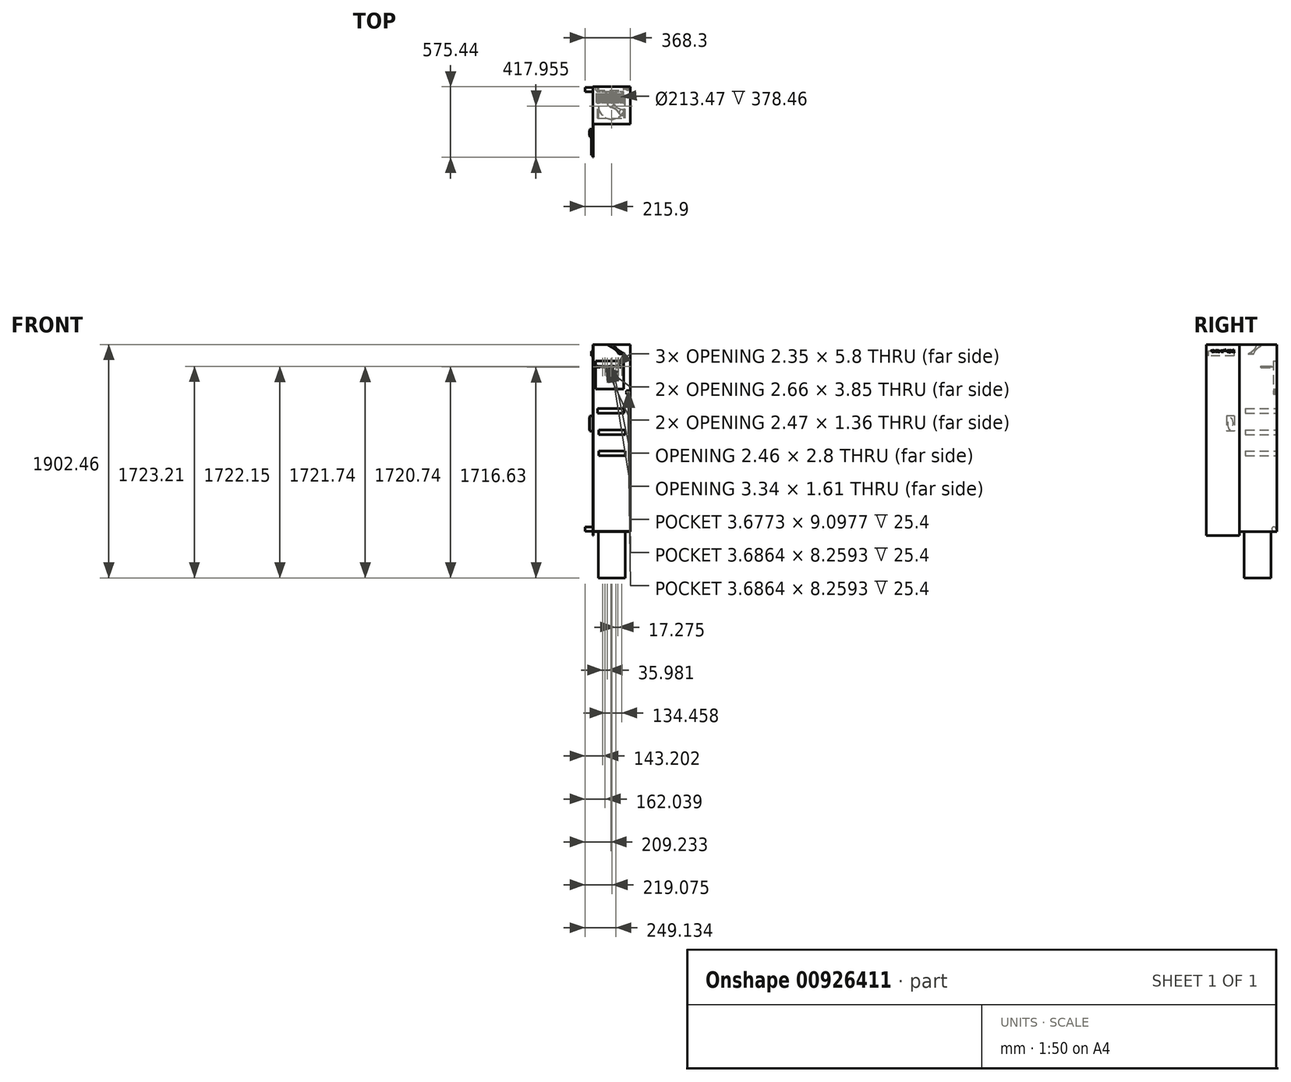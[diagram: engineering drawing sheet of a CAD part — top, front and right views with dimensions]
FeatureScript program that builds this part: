
annotation { "Feature Type Name" : "Feature", "Feature Type Description" : "" }
export const myFeature = defineFeature(function(context is Context, id is Id, definition is map)
    precondition{}
    {
        {
            var Q0;
            Q0=qCreatedBy(makeId("Front.planeOp"),FACE);
            var sketch = newSketch(context, id + "F0", { "sketchPlane" : qUnion([Q0])});
            skLineSegment(sketch, "E0.bottom", {"start": v(152.4, 762) * mm, "end": v(-152.4, 762) * mm});
            skLineSegment(sketch, "E0.top", {"start": v(152.4, -762) * mm, "end": v(-152.4, -762) * mm});
            skLineSegment(sketch, "E0.left", {"start": v(152.4, 762) * mm, "end": v(152.4, -762) * mm});
            skLineSegment(sketch, "E0.right", {"start": v(-152.4, 762) * mm, "end": v(-152.4, -762) * mm});
            skPoint(sketch, "E0.middle", {"position": v(0, 0) * mm});
            skSolve(sketch);
        }
        {
            var Q0;
            Q0=makeQuery(id+"F0.imprint","IMPRINT",FACE,{"disambiguationData":[TD([[makeQuery(id+"F0.imprint","IMPRINT",EDGE,{"derivedFrom":sQuery(id+"F0.wireOp",EDGE,"E0.bottom")}),1.0]])]});
            extrude(context, id + "F1", {"entities" : qUnion([Q0]), "depth" : 304.8 * mm, "offsetDistance" : 25.4 * mm});
        }
        {
            var Q0;
            Q0=makeQuery(id+"F1.opExtrude","CAP_FACE",FACE,{"disambiguationData":[OSD([sQuery(id+"F0.wireOp",EDGE,"E0.bottom"),sQuery(id+"F0.wireOp",EDGE,"E0.top"),sQuery(id+"F0.wireOp",EDGE,"E0.left"),sQuery(id+"F0.wireOp",EDGE,"E0.right")])],"isStart":false});
            shell(context, id + "F2", {"entities" : qUnion([Q0]), "thickness" : 2.54 * mm});
        }
        {
            var Q0;
            Q0=makeQuery(id+"F1.opExtrude","CAP_EDGE",EDGE,{"disambiguationData":[OSD([sQuery(id+"F0.wireOp",EDGE,"E0.right")])],"isStart":false});
            cPlane(context, id + "F3", {"entities" : qUnion([Q0]), "cplaneType" : CPlaneType.LINE_ANGLE, "offset" : 25.4 * mm, "angle" : 0 * degree, "width" : 152.4 * mm, "height" : 152.4 * mm});
        }
        {
            var Q0;
            Q0=qCreatedBy(id+"F3.planeOp",FACE);
            var sketch = newSketch(context, id + "F4", { "sketchPlane" : qUnion([Q0])});
            skLineSegment(sketch, "E1.bottom", {"start": v(304.8, 760.38) * mm, "end": v(575.44, 760.38) * mm});
            skLineSegment(sketch, "E1.top", {"start": v(304.8, -796.06) * mm, "end": v(575.44, -796.06) * mm});
            skLineSegment(sketch, "E1.left", {"start": v(304.8, 760.38) * mm, "end": v(304.8, -796.06) * mm});
            skLineSegment(sketch, "E1.right", {"start": v(575.44, 760.38) * mm, "end": v(575.44, -796.06) * mm});
            skSolve(sketch);
        }
        {
            var Q0;
            Q0=makeQuery(id+"F4.imprint","IMPRINT",FACE,{"disambiguationData":[TD([[makeQuery(id+"F4.imprint","IMPRINT",EDGE,{"derivedFrom":sQuery(id+"F4.wireOp",EDGE,"E1.bottom")}),-1.0]])]});
            extrude(context, id + "F5", {"entities" : qUnion([Q0]), "oppositeDirection" : true, "depth" : 2.54 * mm, "offsetDistance" : 25.4 * mm});
        }
        {
            var Q0;
            Q0=makeQuery(id+"F5.opExtrude","CAP_FACE",FACE,{"disambiguationData":[OSD([sQuery(id+"F4.wireOp",EDGE,"E1.bottom"),sQuery(id+"F4.wireOp",EDGE,"E1.top"),sQuery(id+"F4.wireOp",EDGE,"E1.left"),sQuery(id+"F4.wireOp",EDGE,"E1.right")])],"isStart":true});
            var sketch = newSketch(context, id + "F6", { "sketchPlane" : qUnion([Q0])});
            skSolve(sketch);
        }
        {
            var Q0;
            Q0=makeQuery(id+"F6.imprint","IMPRINT",FACE,{"disambiguationData":[TD([[makeQuery(id+"F6.imprint","IMPRINT",EDGE,{"derivedFrom":makeQuery(id+"F5.opExtrude","CAP_EDGE",EDGE,{"disambiguationData":[OSD([sQuery(id+"F4.wireOp",EDGE,"E1.bottom")])],"isStart":true})}),-1.0]])]});
            var sketch = newSketch(context, id + "F7", { "sketchPlane" : qUnion([Q0])});
            skLineSegment(sketch, "E2.bottom", {"start": v(348.08, 706.14) * mm, "end": v(557.63, 706.14) * mm});
            skLineSegment(sketch, "E2.top", {"start": v(348.08, 668.04) * mm, "end": v(557.63, 668.04) * mm});
            skLineSegment(sketch, "E2.left", {"start": v(348.08, 706.14) * mm, "end": v(348.08, 668.04) * mm});
            skLineSegment(sketch, "E2.right", {"start": v(557.63, 706.14) * mm, "end": v(557.63, 668.04) * mm});
            skSolve(sketch);
        }
        {
            var Q0;
            Q0=makeQuery(id+"F7.imprint","IMPRINT",FACE,{"disambiguationData":[TD([[makeQuery(id+"F7.imprint","IMPRINT",EDGE,{"derivedFrom":sQuery(id+"F7.wireOp",EDGE,"E2.bottom")}),-1.0]])]});
            extrude(context, id + "F8", {"entities" : qUnion([Q0]), "operationType" : NewBodyOperationType.ADD, "depth" : 12.7 * mm, "offsetDistance" : 25.4 * mm});
        }
        {
            var Q0;
            Q0=makeQuery(id+"F8.opExtrude","CAP_FACE",FACE,{"disambiguationData":[OSD([sQuery(id+"F7.wireOp",EDGE,"E2.bottom"),sQuery(id+"F7.wireOp",EDGE,"E2.top"),sQuery(id+"F7.wireOp",EDGE,"E2.left"),sQuery(id+"F7.wireOp",EDGE,"E2.right")])],"isStart":false});
            var sketch = newSketch(context, id + "F9", { "sketchPlane" : qUnion([Q0])});
            skText(sketch, "E3", { "text": "Jorge The Locker", "fontName": "OpenSans-Regular.ttf"});
            const initialGuessF9  = {"E3": [0.34808, 0.70139, 1, 0, 0.01745]};
            skSetInitialGuess(sketch, initialGuessF9);
            skSolve(sketch);
        }
        {
            var Q0;
            Q0 = qSketchRegion(id + "F9", true);
            extrude(context, id + "F10", {"entities" : qUnion([Q0]), "operationType" : NewBodyOperationType.REMOVE, "oppositeDirection" : true, "depth" : 72.64 * mm, "offsetDistance" : 25.4 * mm});
        }
        {
            var Q0;
            Q0=makeQuery(id+"F6.imprint","IMPRINT",FACE,{"disambiguationData":[TD([[makeQuery(id+"F6.imprint","IMPRINT",EDGE,{"derivedFrom":makeQuery(id+"F5.opExtrude","CAP_EDGE",EDGE,{"disambiguationData":[OSD([sQuery(id+"F4.wireOp",EDGE,"E1.bottom")])],"isStart":true})}),-1.0]])]});
            var sketch = newSketch(context, id + "F11", { "sketchPlane" : qUnion([Q0])});
            skLineSegment(sketch, "E4.bottom", {"start": v(347.6, 178.59) * mm, "end": v(411.04, 178.59) * mm});
            skLineSegment(sketch, "E4.top", {"start": v(347.6, 56.18) * mm, "end": v(411.04, 56.18) * mm});
            skLineSegment(sketch, "E4.left", {"start": v(347.6, 178.59) * mm, "end": v(347.6, 56.18) * mm});
            skLineSegment(sketch, "E4.right", {"start": v(411.04, 178.59) * mm, "end": v(411.04, 56.18) * mm});
            skSolve(sketch);
        }
        {
            var Q0;
            Q0 = qSketchRegion(id + "F11", true);
            extrude(context, id + "F12", {"entities" : qUnion([Q0]), "operationType" : NewBodyOperationType.ADD, "depth" : 25.4 * mm, "offsetDistance" : 25.4 * mm});
        }
        {
            var Q0;
            Q0=makeQuery(id+"F12.opExtrude","CAP_FACE",FACE,{"disambiguationData":[OSD([sQuery(id+"F11.wireOp",EDGE,"E4.bottom"),sQuery(id+"F11.wireOp",EDGE,"E4.top"),sQuery(id+"F11.wireOp",EDGE,"E4.left"),sQuery(id+"F11.wireOp",EDGE,"E4.right")])],"isStart":false});
            var sketch = newSketch(context, id + "F13", { "sketchPlane" : qUnion([Q0])});
            skEllipse(sketch, "E5", {"center": v(379.35, 116.15) * mm, "majorRadius": 50.8 * mm, "minorRadius": 19.05 * mm, "majorAxis": v(0, 1)});
            skSolve(sketch);
        }
        {
            var Q0;
            Q0=makeQuery(id+"F13.imprint","IMPRINT",FACE,{"disambiguationData":[TD([[makeQuery(id+"F13.imprint","IMPRINT",EDGE,{"derivedFrom":sQuery(id+"F13.wireOp",EDGE,"E5")}),1.0]])]});
            extrude(context, id + "F14", {"entities" : qUnion([Q0]), "operationType" : NewBodyOperationType.ADD, "depth" : 5.08 * mm, "offsetDistance" : 25.4 * mm});
        }
        {
            var Q0;
            Q0=makeQuery(id+"F2.opShell","OFFSET_FACE",FACE,{"disambiguationData":[OSD([sQuery(id+"F0.wireOp",EDGE,"E0.bottom"),sQuery(id+"F0.wireOp",EDGE,"E0.top"),sQuery(id+"F0.wireOp",EDGE,"E0.left"),sQuery(id+"F0.wireOp",EDGE,"E0.right")])]});
            var sketch = newSketch(context, id + "F15", { "sketchPlane" : qUnion([Q0])});
            skSolve(sketch);
        }
        {
            var Q0;
            Q0=makeQuery(id+"F2.opShell","OFFSET_FACE",FACE,{"disambiguationData":[OSD([sQuery(id+"F0.wireOp",EDGE,"E0.bottom")])]});
            var sketch = newSketch(context, id + "F16", { "sketchPlane" : qUnion([Q0])});
            skCircle(sketch, "E6", {"center": v(-10.16, 141.2) * mm, "radius": 25.4 * mm});
            skSolve(sketch);
        }
        {
            var Q0;
            Q0=makeQuery(id+"F16.imprint","IMPRINT",FACE,{"disambiguationData":[TD([[makeQuery(id+"F16.imprint","IMPRINT",EDGE,{"derivedFrom":sQuery(id+"F16.wireOp",EDGE,"E6")}),-1.0]])]});
            cPlane(context, id + "F17", {"entities" : qUnion([Q0]), "cplaneType" : CPlaneType.OFFSET, "offset" : 76.2 * mm, "width" : 152.4 * mm, "height" : 152.4 * mm});
        }
        {
            var Q0;
            Q0=qCreatedBy(id+"F17.planeOp",FACE);
            var sketch = newSketch(context, id + "F18", { "sketchPlane" : qUnion([Q0])});
            skCircle(sketch, "E7", {"center": v(83.88, 210.58) * mm, "radius": 24.32 * mm});
            skSolve(sketch);
        }
        {
            var Q1;
            Q1=makeQuery(id+"F18.imprint","IMPRINT",FACE,{"disambiguationData":[TD([[makeQuery(id+"F18.imprint","IMPRINT",EDGE,{"derivedFrom":sQuery(id+"F18.wireOp",EDGE,"E7")}),1.0]])]});
            var Q2;
            Q2=makeQuery(id+"F16.imprint","IMPRINT",FACE,{"disambiguationData":[TD([[makeQuery(id+"F16.imprint","IMPRINT",EDGE,{"derivedFrom":sQuery(id+"F16.wireOp",EDGE,"E6")}),1.0]])]});
            loft(context, id + "F19", {"operationType" : NewBodyOperationType.ADD, "sheetProfilesArray" : [{ "sheetProfileEntities" : qUnion([Q1]) }, { "sheetProfileEntities" : qUnion([Q2]) }]});
        }
        {
            var Q0;
            {var subQ0=sQuery(id+"F0.wireOp",EDGE,"E0.bottom");Q0=makeQuery(id+"F15.imprint","IMPRINT",FACE,{"disambiguationData":[TD([[makeQuery(id+"F15.imprint","IMPRINT",EDGE,{"derivedFrom":makeQuery(id+"F2.opShell","OFFSET_EDGE",EDGE,{"disambiguationData":[OSD([subQ0]),TDD([makeQuery(id+"F1.opExtrude","CAP_EDGE",EDGE,{"disambiguationData":[OSD([subQ0])],"isStart":true})])]})}),1.0]])]});}
            var sketch = newSketch(context, id + "F20", { "sketchPlane" : qUnion([Q0])});
            skLineSegment(sketch, "E8.bottom", {"start": v(-130.5, 627.35) * mm, "end": v(98.1, 627.35) * mm});
            skLineSegment(sketch, "E8.top", {"start": v(-130.5, 398.75) * mm, "end": v(98.1, 398.75) * mm});
            skLineSegment(sketch, "E8.left", {"start": v(-130.5, 627.35) * mm, "end": v(-130.5, 398.75) * mm});
            skLineSegment(sketch, "E8.right", {"start": v(98.1, 627.35) * mm, "end": v(98.1, 398.75) * mm});
            skSolve(sketch);
        }
        {
            var Q0;
            Q0=makeQuery(id+"F20.imprint","IMPRINT",FACE,{"disambiguationData":[TD([[makeQuery(id+"F20.imprint","IMPRINT",EDGE,{"derivedFrom":sQuery(id+"F20.wireOp",EDGE,"E8.bottom")}),-1.0]])]});
            extrude(context, id + "F21", {"entities" : qUnion([Q0]), "operationType" : NewBodyOperationType.ADD, "depth" : 25.4 * mm, "offsetDistance" : 25.4 * mm});
        }
        {
            var Q0;
            Q0=makeQuery(id+"F21.opExtrude","CAP_FACE",FACE,{"disambiguationData":[OSD([sQuery(id+"F20.wireOp",EDGE,"E8.bottom"),sQuery(id+"F20.wireOp",EDGE,"E8.top"),sQuery(id+"F20.wireOp",EDGE,"E8.left"),sQuery(id+"F20.wireOp",EDGE,"E8.right")])],"isStart":false});
            var sketch = newSketch(context, id + "F22", { "sketchPlane" : qUnion([Q0])});
            skText(sketch, "E9", { "text": "- Math Homework Pg 975 10-100 Evens", "fontName": "OpenSans-Bold.ttf"});
            const initialGuessF22  = {"E9": [-0.12646, 0.57706, 1, 0, 0.0085]};
            skSetInitialGuess(sketch, initialGuessF22);
            skSolve(sketch);
        }
        {
            var Q0;
            Q0 = qSketchRegion(id + "F22", true);
            extrude(context, id + "F23", {"entities" : qUnion([Q0]), "depth" : 101.6 * mm, "offsetDistance" : 25.4 * mm, "hasSecondDirection" : true, "secondDirectionOppositeDirection" : false, "secondDirectionDepth" : 12.7 * mm});
        }
        {
            var Q0;
            {var subQ0=sQuery(id+"F0.wireOp",EDGE,"E0.bottom");Q0=makeQuery(id+"F15.imprint","IMPRINT",FACE,{"disambiguationData":[TD([[makeQuery(id+"F15.imprint","IMPRINT",EDGE,{"derivedFrom":makeQuery(id+"F2.opShell","OFFSET_EDGE",EDGE,{"disambiguationData":[OSD([subQ0]),TDD([makeQuery(id+"F1.opExtrude","CAP_EDGE",EDGE,{"disambiguationData":[OSD([subQ0])],"isStart":true})])]})}),1.0]])]});}
            var sketch = newSketch(context, id + "F24", { "sketchPlane" : qUnion([Q0])});
            skLineSegment(sketch, "E10.bottom", {"start": v(-114.01, 239.94) * mm, "end": v(101.89, 239.94) * mm});
            skLineSegment(sketch, "E10.top", {"start": v(-114.01, 201.84) * mm, "end": v(101.89, 201.84) * mm});
            skLineSegment(sketch, "E10.left", {"start": v(-114.01, 239.94) * mm, "end": v(-114.01, 201.84) * mm});
            skLineSegment(sketch, "E10.right", {"start": v(101.89, 239.94) * mm, "end": v(101.89, 201.84) * mm});
            skLineSegment(sketch, "E11.bottom", {"start": v(-107.2, 63.73) * mm, "end": v(108.7, 63.73) * mm});
            skLineSegment(sketch, "E11.top", {"start": v(-107.2, 25.63) * mm, "end": v(108.7, 25.63) * mm});
            skLineSegment(sketch, "E11.left", {"start": v(-107.2, 63.73) * mm, "end": v(-107.2, 25.63) * mm});
            skLineSegment(sketch, "E11.right", {"start": v(108.7, 63.73) * mm, "end": v(108.7, 25.63) * mm});
            skLineSegment(sketch, "E12.bottom", {"start": v(-107.2, -106.2) * mm, "end": v(108.7, -106.2) * mm});
            skLineSegment(sketch, "E12.top", {"start": v(-107.2, -144.3) * mm, "end": v(108.7, -144.3) * mm});
            skLineSegment(sketch, "E12.left", {"start": v(-107.2, -106.2) * mm, "end": v(-107.2, -144.3) * mm});
            skLineSegment(sketch, "E12.right", {"start": v(108.7, -106.2) * mm, "end": v(108.7, -144.3) * mm});
            skSolve(sketch);
        }
        {
            var Q0;
            Q0=makeQuery(id+"F24.imprint","IMPRINT",FACE,{"disambiguationData":[TD([[makeQuery(id+"F24.imprint","IMPRINT",EDGE,{"derivedFrom":sQuery(id+"F24.wireOp",EDGE,"E12.bottom")}),-1.0]])]});
            var Q1;
            Q1=makeQuery(id+"F24.imprint","IMPRINT",FACE,{"disambiguationData":[TD([[makeQuery(id+"F24.imprint","IMPRINT",EDGE,{"derivedFrom":sQuery(id+"F24.wireOp",EDGE,"E11.bottom")}),-1.0]])]});
            var Q2;
            Q2=makeQuery(id+"F24.imprint","IMPRINT",FACE,{"disambiguationData":[TD([[makeQuery(id+"F24.imprint","IMPRINT",EDGE,{"derivedFrom":sQuery(id+"F24.wireOp",EDGE,"E10.bottom")}),-1.0]])]});
            extrude(context, id + "F25", {"entities" : qUnion([Q0, Q1, Q2]), "operationType" : NewBodyOperationType.ADD, "depth" : 254 * mm, "offsetDistance" : 25.4 * mm});
        }
        {
            var Q0;
            Q0=makeQuery(id+"F2.opShell","OFFSET_FACE",FACE,{"disambiguationData":[OSD([sQuery(id+"F0.wireOp",EDGE,"E0.top")])]});
            var sketch = newSketch(context, id + "F26", { "sketchPlane" : qUnion([Q0])});
            skCircle(sketch, "E13", {"center": v(0, -157.49) * mm, "radius": 109.28 * mm});
            skSolve(sketch);
        }
        {
            var Q0;
            Q0 = qSketchRegion(id + "F26", true);
            extrude(context, id + "F27", {"entities" : qUnion([Q0]), "operationType" : NewBodyOperationType.ADD, "oppositeDirection" : true, "depth" : 381 * mm, "offsetDistance" : 25.4 * mm});
        }
        {
            var Q0;
            Q0=makeQuery(id+"F27.opExtrude","CAP_FACE",FACE,{"disambiguationData":[OSD([sQuery(id+"F26.wireOp",EDGE,"E13")])],"isStart":false});
            shell(context, id + "F28", {"entities" : qUnion([Q0]), "thickness" : 2.54 * mm});
        }
        {
            var Q0;
            {var subQ0=sQuery(id+"F0.wireOp",EDGE,"E0.bottom");Q0=makeQuery(id+"F15.imprint","IMPRINT",FACE,{"disambiguationData":[TD([[makeQuery(id+"F15.imprint","IMPRINT",EDGE,{"derivedFrom":makeQuery(id+"F2.opShell","OFFSET_EDGE",EDGE,{"disambiguationData":[OSD([subQ0]),TDD([makeQuery(id+"F1.opExtrude","CAP_EDGE",EDGE,{"disambiguationData":[OSD([subQ0])],"isStart":true})])]})}),1.0]])]});}
            var sketch = newSketch(context, id + "F29", { "sketchPlane" : qUnion([Q0])});
            skLineSegment(sketch, "E14.bottom", {"start": v(149.79, 386.38) * mm, "end": v(119.02, 386.38) * mm});
            skLineSegment(sketch, "E14.top", {"start": v(149.79, 357.03) * mm, "end": v(119.02, 357.03) * mm});
            skLineSegment(sketch, "E14.left", {"start": v(149.79, 386.38) * mm, "end": v(149.79, 357.03) * mm});
            skLineSegment(sketch, "E14.right", {"start": v(119.02, 386.38) * mm, "end": v(119.02, 357.03) * mm});
            skSolve(sketch);
        }
        {
            var Q0;
            Q0 = qSketchRegion(id + "F29", true);
            extrude(context, id + "F30", {"entities" : qUnion([Q0]), "operationType" : NewBodyOperationType.ADD, "depth" : 25.4 * mm, "offsetDistance" : 25.4 * mm});
        }
        {
            var Q0;
            Q0=makeQuery(id+"F30.opExtrude","CAP_FACE",FACE,{"disambiguationData":[OSD([sQuery(id+"F29.wireOp",EDGE,"E14.bottom"),sQuery(id+"F29.wireOp",EDGE,"E14.top"),sQuery(id+"F29.wireOp",EDGE,"E14.left"),sQuery(id+"F29.wireOp",EDGE,"E14.right")])],"isStart":false});
            var sketch = newSketch(context, id + "F31", { "sketchPlane" : qUnion([Q0])});
            skLineSegment(sketch, "E15.bottom", {"start": v(124.07, 377.2) * mm, "end": v(127.76, 377.2) * mm});
            skLineSegment(sketch, "E15.top", {"start": v(124.07, 368.94) * mm, "end": v(127.76, 368.94) * mm});
            skLineSegment(sketch, "E15.left", {"start": v(124.07, 377.2) * mm, "end": v(124.07, 368.94) * mm});
            skLineSegment(sketch, "E15.right", {"start": v(127.76, 377.2) * mm, "end": v(127.76, 368.94) * mm});
            skLineSegment(sketch, "E16.bottom", {"start": v(132.23, 376.88) * mm, "end": v(135.92, 376.88) * mm});
            skLineSegment(sketch, "E16.top", {"start": v(132.23, 368.62) * mm, "end": v(135.92, 368.62) * mm});
            skLineSegment(sketch, "E16.left", {"start": v(132.23, 376.88) * mm, "end": v(132.23, 368.62) * mm});
            skLineSegment(sketch, "E16.right", {"start": v(135.92, 376.88) * mm, "end": v(135.92, 368.62) * mm});
            skLineSegment(sketch, "E17.bottom", {"start": v(141.35, 376.88) * mm, "end": v(145.03, 376.88) * mm});
            skLineSegment(sketch, "E17.top", {"start": v(141.35, 367.78) * mm, "end": v(145.03, 367.78) * mm});
            skLineSegment(sketch, "E17.left", {"start": v(141.35, 376.88) * mm, "end": v(141.35, 367.78) * mm});
            skLineSegment(sketch, "E17.right", {"start": v(145.03, 376.88) * mm, "end": v(145.03, 367.78) * mm});
            skSolve(sketch);
        }
        {
            var Q0;
            Q0 = qSketchRegion(id + "F31", true);
            extrude(context, id + "F32", {"entities" : qUnion([Q0]), "operationType" : NewBodyOperationType.REMOVE, "oppositeDirection" : true, "depth" : 25.4 * mm, "offsetDistance" : 25.4 * mm});
        }
        {
            var Q0;
            Q0=makeQuery(id+"F2.opShell","OFFSET_FACE",FACE,{"disambiguationData":[OSD([sQuery(id+"F0.wireOp",EDGE,"E0.right")])]});
            var sketch = newSketch(context, id + "F33", { "sketchPlane" : qUnion([Q0])});
            skCircle(sketch, "E18", {"center": v(-23.72, -742.18) * mm, "radius": 17.28 * mm});
            skSolve(sketch);
        }
        {
            var Q0;
            Q0 = qSketchRegion(id + "F33", true);
            extrude(context, id + "F34", {"entities" : qUnion([Q0]), "operationType" : NewBodyOperationType.ADD, "oppositeDirection" : true, "depth" : 66.04 * mm, "offsetDistance" : 25.4 * mm});
        }
    });
